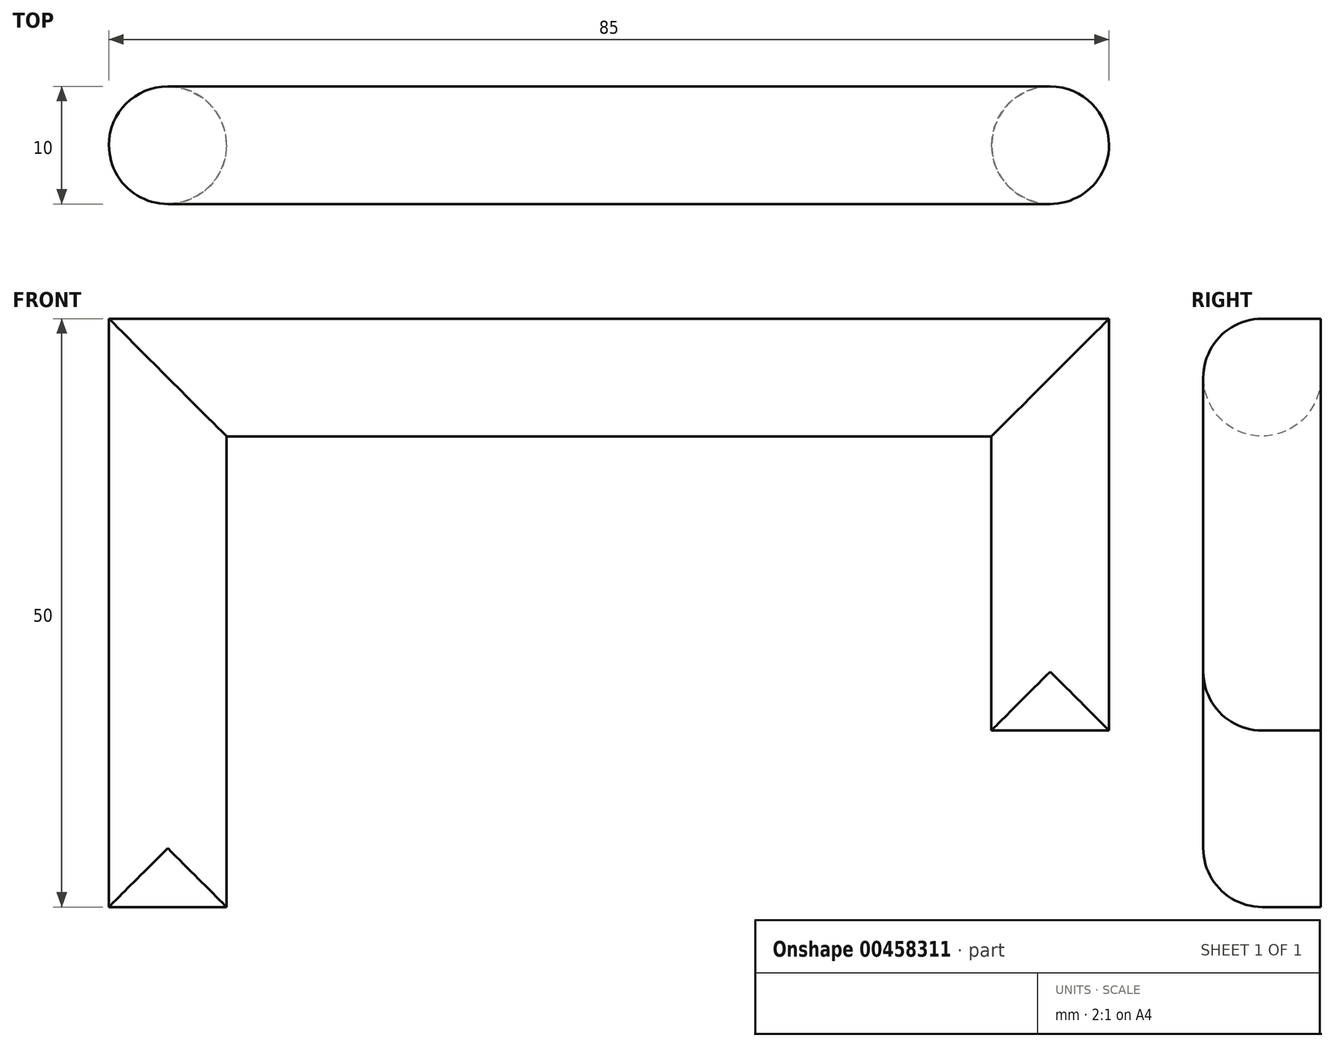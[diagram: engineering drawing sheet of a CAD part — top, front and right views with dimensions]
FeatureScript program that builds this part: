
annotation { "Feature Type Name" : "Feature", "Feature Type Description" : "" }
export const myFeature = defineFeature(function(context is Context, id is Id, definition is map)
    precondition{}
    {
        {
            var Q0;
            Q0=qCreatedBy(makeId("Top.planeOp"),FACE);
            var sketch = newSketch(context, id + "F0", { "sketchPlane" : qUnion([Q0])});
            skLineSegment(sketch, "E0.bottom", {"start": v(0, 0) * mm, "end": v(10, 0) * mm});
            skLineSegment(sketch, "E0.top", {"start": v(0, 10) * mm, "end": v(10, 10) * mm});
            skLineSegment(sketch, "E0.left", {"start": v(0, 0) * mm, "end": v(0, 10) * mm});
            skLineSegment(sketch, "E0.right", {"start": v(10, 0) * mm, "end": v(10, 10) * mm});
            skSolve(sketch);
        }
        {
            var Q0;
            Q0=makeQuery(id+"F0.imprint","IMPRINT",FACE,{"disambiguationData":[TD([[makeQuery(id+"F0.imprint","IMPRINT",EDGE,{"derivedFrom":sQuery(id+"F0.wireOp",EDGE,"E0.bottom")}),1.0]])]});
            extrude(context, id + "F1", {"entities" : qUnion([Q0]), "depth" : 50 * mm});
        }
        {
            var Q0;
            Q0=makeQuery(id+"F1.opExtrude","SWEPT_FACE",FACE,{"disambiguationData":[OSD([sQuery(id+"F0.wireOp",EDGE,"E0.right")])]});
            var sketch = newSketch(context, id + "F2", { "sketchPlane" : qUnion([Q0])});
            skLineSegment(sketch, "E1.bottom", {"start": v(0, 50) * mm, "end": v(10, 50) * mm});
            skLineSegment(sketch, "E1.top", {"start": v(0, 40) * mm, "end": v(10, 40) * mm});
            skLineSegment(sketch, "E1.left", {"start": v(0, 50) * mm, "end": v(0, 40) * mm});
            skLineSegment(sketch, "E1.right", {"start": v(10, 50) * mm, "end": v(10, 40) * mm});
            skSolve(sketch);
        }
        {
            var Q0;
            Q0=makeQuery(id+"F2.imprint","IMPRINT",FACE,{"disambiguationData":[TD([[makeQuery(id+"F2.imprint","IMPRINT",EDGE,{"derivedFrom":sQuery(id+"F2.wireOp",EDGE,"E1.bottom")}),-1.0]])]});
            extrude(context, id + "F3", {"entities" : qUnion([Q0]), "operationType" : NewBodyOperationType.ADD, "depth" : 75 * mm});
        }
        {
            var Q0;
            Q0=makeQuery(id+"F3.opExtrude","SWEPT_FACE",FACE,{"disambiguationData":[OSD([sQuery(id+"F2.wireOp",EDGE,"E1.top")])]});
            var sketch = newSketch(context, id + "F4", { "sketchPlane" : qUnion([Q0])});
            skLineSegment(sketch, "E2.bottom", {"start": v(85, 0) * mm, "end": v(75, 0) * mm});
            skLineSegment(sketch, "E2.top", {"start": v(85, -10) * mm, "end": v(75, -10) * mm});
            skLineSegment(sketch, "E2.left", {"start": v(85, 0) * mm, "end": v(85, -10) * mm});
            skLineSegment(sketch, "E2.right", {"start": v(75, 0) * mm, "end": v(75, -10) * mm});
            skSolve(sketch);
        }
        {
            var Q0;
            Q0=makeQuery(id+"F4.imprint","IMPRINT",FACE,{"disambiguationData":[TD([[makeQuery(id+"F4.imprint","IMPRINT",EDGE,{"derivedFrom":sQuery(id+"F4.wireOp",EDGE,"E2.bottom")}),1.0]])]});
            extrude(context, id + "F5", {"entities" : qUnion([Q0]), "operationType" : NewBodyOperationType.ADD, "depth" : 25 * mm});
        }
        {
            var Q0;
            Q0=makeQuery(id+"F1.opExtrude","SWEPT_EDGE",EDGE,{"disambiguationData":[OSD([sQuery(id+"F0.wireOp",EDGE,"E0.bottom"),sQuery(id+"F0.wireOp",EDGE,"E0.right")])]});
            var Q1;
            Q1=makeQuery(id+"F1.opExtrude","SWEPT_EDGE",EDGE,{"disambiguationData":[OSD([sQuery(id+"F0.wireOp",EDGE,"E0.bottom"),sQuery(id+"F0.wireOp",EDGE,"E0.left")])]});
            var Q2;
            Q2=makeQuery(id+"F1.opExtrude","SWEPT_EDGE",EDGE,{"disambiguationData":[OSD([sQuery(id+"F0.wireOp",EDGE,"E0.top"),sQuery(id+"F0.wireOp",EDGE,"E0.left")])]});
            var Q3;
            Q3=makeQuery(id+"F1.opExtrude","SWEPT_EDGE",EDGE,{"disambiguationData":[OSD([sQuery(id+"F0.wireOp",EDGE,"E0.top"),sQuery(id+"F0.wireOp",EDGE,"E0.right")])]});
            var Q4;
            Q4=makeQuery(id+"F3.boolean.opBoolean","MERGE",EDGE,{"derivedFrom":[makeQuery(id+"F1.opExtrude","CAP_EDGE",EDGE,{"disambiguationData":[OSD([sQuery(id+"F0.wireOp",EDGE,"E0.bottom")])],"isStart":false}),makeQuery(id+"F3.opExtrude","SWEPT_EDGE",EDGE,{"disambiguationData":[OSD([sQuery(id+"F2.wireOp",EDGE,"E1.bottom"),sQuery(id+"F2.wireOp",EDGE,"E1.left")])]})]});
            var Q5;
            Q5=makeQuery(id+"F3.opExtrude","SWEPT_EDGE",EDGE,{"disambiguationData":[OSD([sQuery(id+"F0.wireOp",EDGE,"E0.bottom"),sQuery(id+"F0.wireOp",EDGE,"E0.right"),sQuery(id+"F2.wireOp",EDGE,"E1.top"),sQuery(id+"F2.wireOp",EDGE,"E1.left")])]});
            var Q6;
            Q6=makeQuery(id+"F3.opExtrude","SWEPT_EDGE",EDGE,{"disambiguationData":[OSD([sQuery(id+"F0.wireOp",EDGE,"E0.top"),sQuery(id+"F0.wireOp",EDGE,"E0.right"),sQuery(id+"F2.wireOp",EDGE,"E1.top"),sQuery(id+"F2.wireOp",EDGE,"E1.right")])]});
            var Q7;
            Q7=makeQuery(id+"F5.opExtrude","SWEPT_EDGE",EDGE,{"disambiguationData":[OSD([sQuery(id+"F0.wireOp",EDGE,"E0.top"),sQuery(id+"F0.wireOp",EDGE,"E0.right"),sQuery(id+"F2.wireOp",EDGE,"E1.top"),sQuery(id+"F2.wireOp",EDGE,"E1.right"),sQuery(id+"F4.wireOp",EDGE,"E2.top"),sQuery(id+"F4.wireOp",EDGE,"E2.right")])]});
            var Q8;
            Q8=makeQuery(id+"F5.boolean.opBoolean","MERGE",EDGE,{"derivedFrom":[makeQuery(id+"F3.opExtrude","CAP_EDGE",EDGE,{"disambiguationData":[OSD([sQuery(id+"F2.wireOp",EDGE,"E1.left")])],"isStart":false}),makeQuery(id+"F5.opExtrude","SWEPT_EDGE",EDGE,{"disambiguationData":[OSD([sQuery(id+"F4.wireOp",EDGE,"E2.bottom"),sQuery(id+"F4.wireOp",EDGE,"E2.left")])]})]});
            var Q9;
            Q9=makeQuery(id+"F5.boolean.opBoolean","MERGE",FACE,{"derivedFrom":[makeQuery(id+"F3.boolean.opBoolean","MERGE",FACE,{"derivedFrom":[makeQuery(id+"F1.opExtrude","SWEPT_FACE",FACE,{"disambiguationData":[OSD([sQuery(id+"F0.wireOp",EDGE,"E0.bottom")])]}),makeQuery(id+"F3.opExtrude","SWEPT_FACE",FACE,{"disambiguationData":[OSD([sQuery(id+"F2.wireOp",EDGE,"E1.left")])]})]}),makeQuery(id+"F5.opExtrude","SWEPT_FACE",FACE,{"disambiguationData":[OSD([sQuery(id+"F4.wireOp",EDGE,"E2.bottom")])]})]});
            var Q10;
            Q10=makeQuery(id+"F5.boolean.opBoolean","MERGE",EDGE,{"derivedFrom":[makeQuery(id+"F3.opExtrude","CAP_EDGE",EDGE,{"disambiguationData":[OSD([sQuery(id+"F2.wireOp",EDGE,"E1.right")])],"isStart":false}),makeQuery(id+"F5.opExtrude","SWEPT_EDGE",EDGE,{"disambiguationData":[OSD([sQuery(id+"F4.wireOp",EDGE,"E2.top"),sQuery(id+"F4.wireOp",EDGE,"E2.left")])]})]});
            fillet(context, id + "F6", {"entities" : qUnion([Q0, Q1, Q2, Q3, Q4, Q5, Q6, Q7, Q8, Q9, Q10]), "radius" : 5 * mm, "tangentPropagation" : true, "allowEdgeOverflow" : false});
        }
    });
